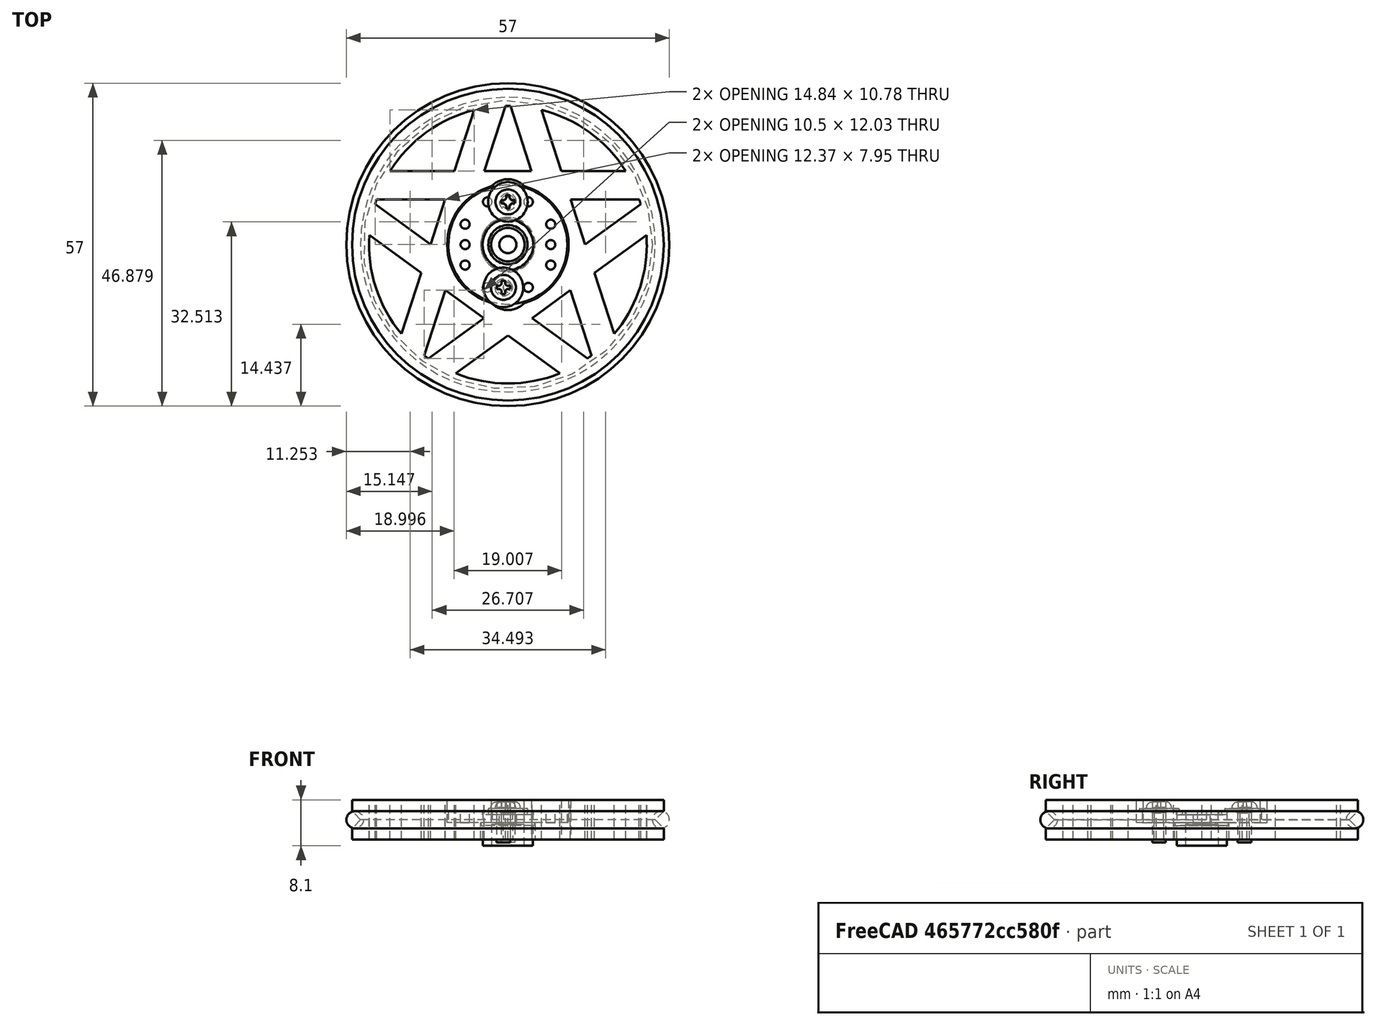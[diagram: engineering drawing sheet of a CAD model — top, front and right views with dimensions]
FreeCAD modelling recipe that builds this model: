
FCSTD DOCUMENT  (FreeCAD 0.14R3702 (Git))
Label: Renacuajo-wheel-pentacle-assembly
License: CC-BY 3.0
LicenseURL: http://creativecommons.org/licenses/by/3.0/
objects: Part::Feature×4, Part::Torus×1, Part::Compound×1
note: 6 computed .brp shape members not serialized (recipe doc carries the construction recipe); baked Part::Feature solids carry a one-line shape summary decoded from their .brp

FEATURE [Part::Feature] PolarPattern  label="Renacuajo-wheel-pentacle-final"
  shape: bbox 55 x 55 x 7 mm, 51 faces (baked)
FEATURE [Part::Torus] Torus  label="o-ring"
  Angle1 = -180
  Angle2 = 180
  Angle3 = 360
  Radius1 = 27
  Radius2 = 1.5
FEATURE [Part::Feature] Pocket  label="small-rounded-horn"
  Placement = pos=(0,0,-0.5) rot=(0,0,1;0rad)
  shape: bbox 21 x 21 x 6.2 mm, 28 faces (baked)
FEATURE [Part::Feature] Chamfer002  label="screw-1"
  Placement = pos=(-0.8,-7.55,1.5) rot=(0,0,1;0rad)
  shape: bbox 7 x 7 x 7.14 mm, 33 faces (baked)
FEATURE [Part::Feature] Chamfer003  label="screw-2"
  Placement = pos=(0,7.55,1.5) rot=(0,0,1;0rad)
  shape: bbox 7 x 7 x 7.14 mm, 33 faces (baked)
FEATURE [Part::Compound] Compound  label="Renacuajo-wheel-pentacle-assembly-final"
  Links = -> [PolarPattern,Torus,Pocket,Chamfer002,Chamfer003]
